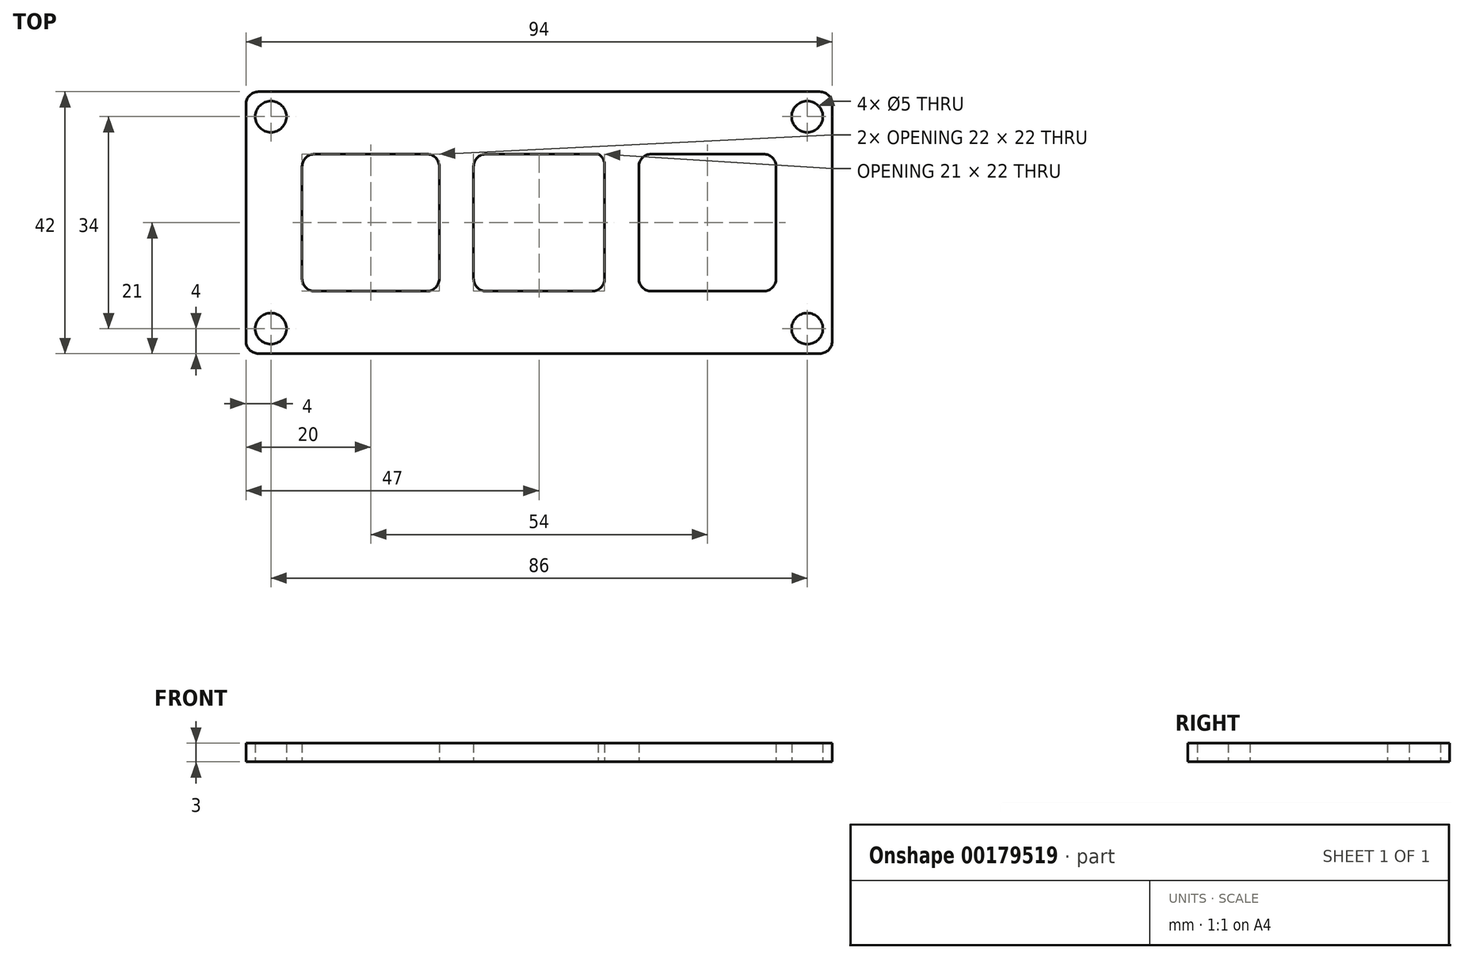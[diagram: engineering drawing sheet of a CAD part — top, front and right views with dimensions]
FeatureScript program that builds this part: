
annotation { "Feature Type Name" : "Feature", "Feature Type Description" : "" }
export const myFeature = defineFeature(function(context is Context, id is Id, definition is map)
    precondition{}
    {
        {
            var Q0;
            Q0=qCreatedBy(makeId("Top.planeOp"),FACE);
            var sketch = newSketch(context, id + "F0", { "sketchPlane" : qUnion([Q0])});
            skLineSegment(sketch, "E0.bottom", {"start": v(47, 0) * mm, "end": v(-43, 0) * mm});
            skLineSegment(sketch, "E0.top", {"start": v(47, 42) * mm, "end": v(-43, 42) * mm});
            skLineSegment(sketch, "E0.left", {"start": v(49, 2) * mm, "end": v(49, 40) * mm});
            skLineSegment(sketch, "E0.right", {"start": v(-45, 2) * mm, "end": v(-45, 40) * mm});
            skLineSegment(sketch, "E1.bottom", {"start": v(-34, 32) * mm, "end": v(-16, 32) * mm});
            skLineSegment(sketch, "E1.top", {"start": v(-34, 10) * mm, "end": v(-16, 10) * mm});
            skLineSegment(sketch, "E1.left", {"start": v(-36, 30) * mm, "end": v(-36, 12) * mm});
            skLineSegment(sketch, "E1.right", {"start": v(-14, 30) * mm, "end": v(-14, 12) * mm});
            skLineSegment(sketch, "E2.bottom", {"start": v(20, 32) * mm, "end": v(38, 32) * mm});
            skLineSegment(sketch, "E2.top", {"start": v(20, 10) * mm, "end": v(38, 10) * mm});
            skLineSegment(sketch, "E2.left", {"start": v(18, 30) * mm, "end": v(18, 12) * mm});
            skLineSegment(sketch, "E2.right", {"start": v(40, 30) * mm, "end": v(40, 12) * mm});
            skLineSegment(sketch, "E3.left", {"start": v(-10.4, -34.5) * mm, "end": v(-10.4, -34.5) * mm});
            skLineSegment(sketch, "E3.right", {"start": v(9.6, -34.5) * mm, "end": v(9.6, -34.5) * mm});
            skPoint(sketch, "E4.visualSharp", {"position": v(-45, 42) * mm});
            skArc(sketch, "E4.filletArc", {"start": v(-43, 42) * mm, "mid": v(-44.41, 41.41) * mm, "end": v(-45, 40) * mm});
            skPoint(sketch, "E5.visualSharp", {"position": v(49, 42) * mm});
            skArc(sketch, "E5.filletArc", {"start": v(49, 40) * mm, "mid": v(48.41, 41.41) * mm, "end": v(47, 42) * mm});
            skPoint(sketch, "E6.visualSharp", {"position": v(49, 0) * mm});
            skArc(sketch, "E6.filletArc", {"start": v(47, 0) * mm, "mid": v(48.41, 0.59) * mm, "end": v(49, 2) * mm});
            skPoint(sketch, "E7.visualSharp", {"position": v(-45, 0) * mm});
            skArc(sketch, "E7.filletArc", {"start": v(-45, 2) * mm, "mid": v(-44.41, 0.59) * mm, "end": v(-43, 0) * mm});
            skPoint(sketch, "E8.visualSharp", {"position": v(40, 31) * mm});
            skArc(sketch, "E8.filletArc", {"start": v(40, 30) * mm, "mid": v(39.41, 31.41) * mm, "end": v(38, 32) * mm});
            skPoint(sketch, "E9.visualSharp", {"position": v(40, 10) * mm});
            skArc(sketch, "E9.filletArc", {"start": v(38, 10) * mm, "mid": v(39.41, 10.59) * mm, "end": v(40, 12) * mm});
            skPoint(sketch, "E10.visualSharp", {"position": v(18, 10) * mm});
            skArc(sketch, "E10.filletArc", {"start": v(18, 12) * mm, "mid": v(18.59, 10.59) * mm, "end": v(20, 10) * mm});
            skPoint(sketch, "E11.visualSharp", {"position": v(18, 32) * mm});
            skArc(sketch, "E11.filletArc", {"start": v(20, 32) * mm, "mid": v(18.59, 31.41) * mm, "end": v(18, 30) * mm});
            skPoint(sketch, "E12.visualSharp", {"position": v(-37, 32) * mm});
            skArc(sketch, "E12.filletArc", {"start": v(-34, 32) * mm, "mid": v(-35.41, 31.41) * mm, "end": v(-36, 30) * mm});
            skPoint(sketch, "E13.visualSharp", {"position": v(-36, 10) * mm});
            skArc(sketch, "E13.filletArc", {"start": v(-36, 12) * mm, "mid": v(-35.41, 10.59) * mm, "end": v(-34, 10) * mm});
            skPoint(sketch, "E14.visualSharp", {"position": v(-14, 10) * mm});
            skArc(sketch, "E14.filletArc", {"start": v(-16, 10) * mm, "mid": v(-14.59, 10.59) * mm, "end": v(-14, 12) * mm});
            skPoint(sketch, "E15.visualSharp", {"position": v(-14, 32) * mm});
            skArc(sketch, "E15.filletArc", {"start": v(-14, 30) * mm, "mid": v(-14.59, 31.41) * mm, "end": v(-16, 32) * mm});
            skCircle(sketch, "E16", {"center": v(-41, 4) * mm, "radius": 2.5 * mm});
            skCircle(sketch, "E17", {"center": v(45, 4) * mm, "radius": 2.5 * mm});
            skCircle(sketch, "E18", {"center": v(45, 38) * mm, "radius": 2.5 * mm});
            skCircle(sketch, "E19", {"center": v(-41, 38) * mm, "radius": 2.5 * mm});
            skLineSegment(sketch, "E20.bottom", {"start": v(-6.5, 32) * mm, "end": v(11.5, 32) * mm});
            skLineSegment(sketch, "E20.top", {"start": v(-6.5, 10) * mm, "end": v(10.5, 10) * mm});
            skLineSegment(sketch, "E20.left", {"start": v(-8.5, 30) * mm, "end": v(-8.5, 12) * mm});
            skLineSegment(sketch, "E20.right", {"start": v(12.5, 30.27) * mm, "end": v(12.5, 12) * mm});
            skPoint(sketch, "E21.visualSharp", {"position": v(-8.5, 32) * mm});
            skArc(sketch, "E21.filletArc", {"start": v(-6.5, 32) * mm, "mid": v(-7.91, 31.41) * mm, "end": v(-8.5, 30) * mm});
            skPoint(sketch, "E22.visualSharp", {"position": v(-8.5, 10) * mm});
            skArc(sketch, "E22.filletArc", {"start": v(-8.5, 12) * mm, "mid": v(-7.91, 10.59) * mm, "end": v(-6.5, 10) * mm});
            skPoint(sketch, "E23.visualSharp", {"position": v(12.5, 10) * mm});
            skArc(sketch, "E23.filletArc", {"start": v(10.5, 10) * mm, "mid": v(11.91, 10.59) * mm, "end": v(12.5, 12) * mm});
            skPoint(sketch, "E24.visualSharp", {"position": v(12.5, 31) * mm});
            skArc(sketch, "E24.filletArc", {"start": v(12.5, 30.27) * mm, "mid": v(12.23, 31.27) * mm, "end": v(11.5, 32) * mm});
            skSolve(sketch);
        }
        {
            var Q0;
            Q0=makeQuery(id+"F0.imprint","IMPRINT",FACE,{"disambiguationData":[TD([[makeQuery(id+"F0.imprint","IMPRINT",EDGE,{"derivedFrom":sQuery(id+"F0.wireOp",EDGE,"E0.bottom")}),-1.0]])]});
            extrude(context, id + "F1", {"entities" : qUnion([Q0]), "depth" : 3 * mm});
        }
    });
